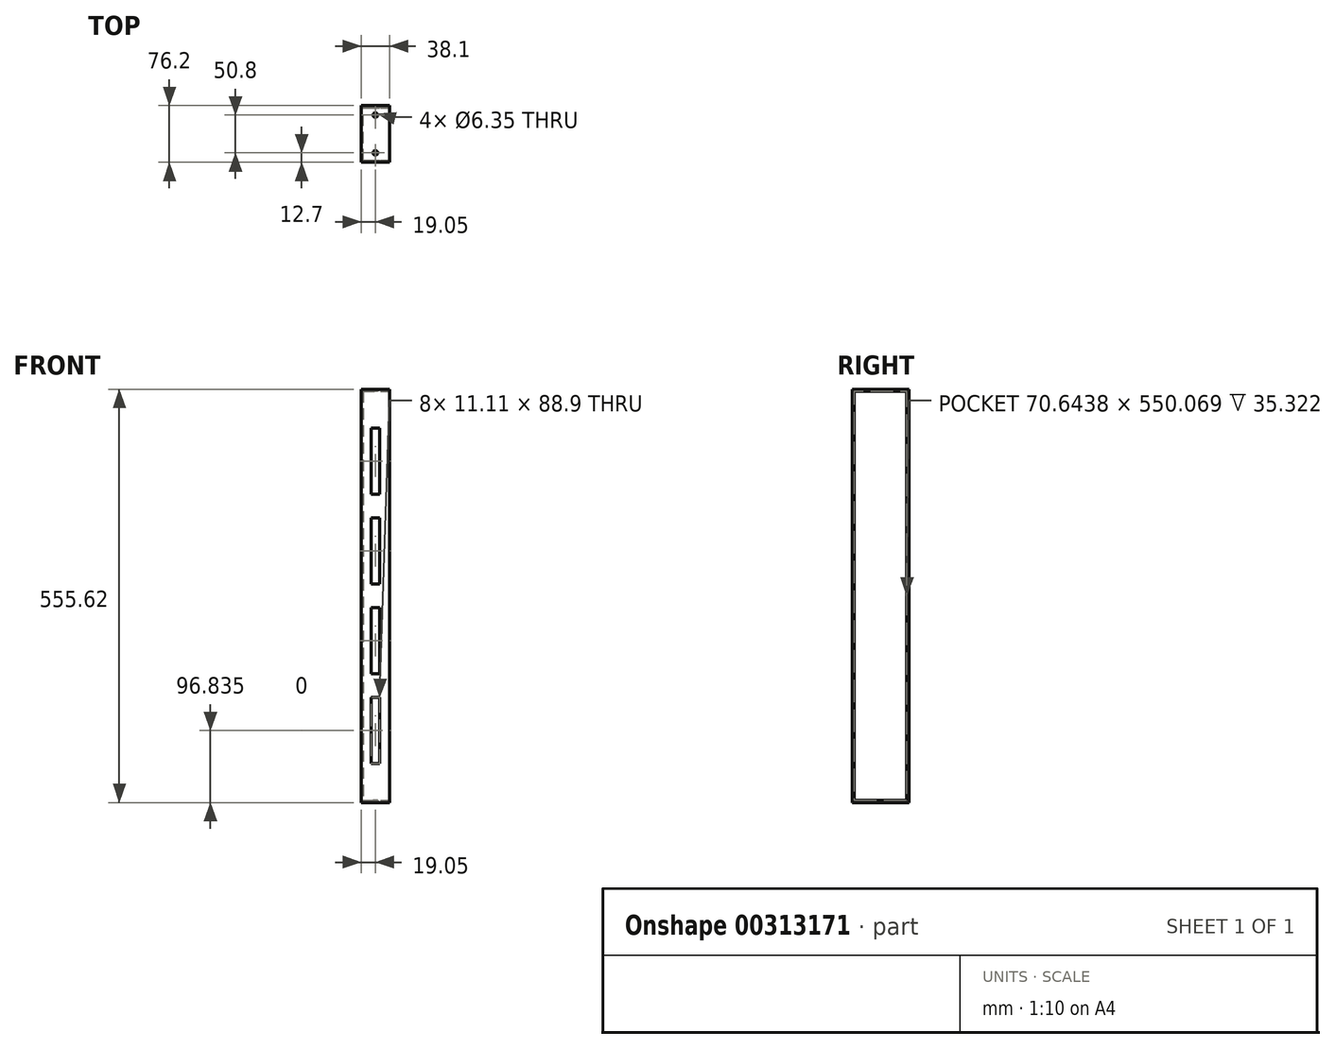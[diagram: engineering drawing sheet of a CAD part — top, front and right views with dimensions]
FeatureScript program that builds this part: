
annotation { "Feature Type Name" : "Feature", "Feature Type Description" : "" }
export const myFeature = defineFeature(function(context is Context, id is Id, definition is map)
    precondition{}
    {
        {
            var Q0;
            Q0=qCreatedBy(makeId("Top.planeOp"),FACE);
            var sketch = newSketch(context, id + "F0", { "sketchPlane" : qUnion([Q0])});
            skLineSegment(sketch, "E0.bottom", {"start": v(0, 0) * mm, "end": v(38.1, 0) * mm});
            skLineSegment(sketch, "E0.top", {"start": v(0, 76.2) * mm, "end": v(38.1, 76.2) * mm});
            skLineSegment(sketch, "E0.left", {"start": v(0, 0) * mm, "end": v(0, 76.2) * mm});
            skLineSegment(sketch, "E0.right", {"start": v(38.1, 0) * mm, "end": v(38.1, 76.2) * mm});
            skSolve(sketch);
        }
        {
            var Q0;
            Q0=qSketchRegion(id+"F0",true);
            extrude(context, id + "F1", {"entities" : qUnion([Q0]), "endBound" : BoundingType.SYMMETRIC, "depth" : 555.62 * mm});
        }
        {
            var Q0;
            Q0=makeQuery(id+"F1.opExtrude","SWEPT_FACE",FACE,{"disambiguationData":[OSD([sQuery(id+"F0.wireOp",EDGE,"E0.right")])]});
            shell(context, id + "F2", {"entities" : qUnion([Q0]), "thickness" : 2.78 * mm});
        }
        {
            var Q0;
            Q0=makeQuery(id+"F1.opExtrude","CAP_FACE",FACE,{"disambiguationData":[OSD([sQuery(id+"F0.wireOp",EDGE,"E0.bottom"),sQuery(id+"F0.wireOp",EDGE,"E0.top"),sQuery(id+"F0.wireOp",EDGE,"E0.left"),sQuery(id+"F0.wireOp",EDGE,"E0.right")])],"isStart":true});
            var sketch = newSketch(context, id + "F3", { "sketchPlane" : qUnion([Q0])});
            skCircle(sketch, "E1", {"center": v(19.05, -12.7) * mm, "radius": 3.18 * mm});
            skPoint(sketch, "E1.centerSnap0", {"position": v(19.05, 0) * mm});
            skCircle(sketch, "E2", {"center": v(19.05, -63.5) * mm, "radius": 3.18 * mm});
            skSolve(sketch);
        }
        {
            var Q0;
            Q0=qSketchRegion(id+"F3",true);
            extrude(context, id + "F4", {"entities" : qUnion([Q0]), "operationType" : NewBodyOperationType.REMOVE, "endBound" : BoundingType.THROUGH_ALL, "oppositeDirection" : true, "depth" : 25.4 * mm});
        }
        {
            var Q0;
            Q0=makeQuery(id+"F1.opExtrude","SWEPT_FACE",FACE,{"disambiguationData":[OSD([sQuery(id+"F0.wireOp",EDGE,"E0.bottom")])]});
            var sketch = newSketch(context, id + "F5", { "sketchPlane" : qUnion([Q0])});
            skLineSegment(sketch, "E3.bottom", {"start": v(24.6, -225.43) * mm, "end": v(13.5, -225.43) * mm});
            skLineSegment(sketch, "E3.top", {"start": v(24.6, -136.53) * mm, "end": v(13.5, -136.53) * mm});
            skLineSegment(sketch, "E3.left", {"start": v(24.6, -225.43) * mm, "end": v(24.6, -136.53) * mm});
            skLineSegment(sketch, "E3.right", {"start": v(13.5, -225.43) * mm, "end": v(13.5, -136.53) * mm});
            skPoint(sketch, "E3.middle", {"position": v(19.05, -180.97) * mm});
            skPoint(sketch, "E3.middle.positionSnap0", {"position": v(19.05, -277.81) * mm});
            skPoint(sketch, "E3.centerSnap0", {"position": v(19.05, -277.81) * mm});
            skLineSegment(sketch, "E4.0.1.0", {"start": v(24.6, -104.78) * mm, "end": v(13.5, -104.78) * mm});
            skPoint(sketch, "E4.0.1.1", {"position": v(19.05, -60.33) * mm});
            skLineSegment(sketch, "E4.0.1.2", {"start": v(13.5, -104.78) * mm, "end": v(13.5, -15.88) * mm});
            skLineSegment(sketch, "E4.0.1.3", {"start": v(24.6, -104.78) * mm, "end": v(24.6, -15.88) * mm});
            skLineSegment(sketch, "E4.0.1.4", {"start": v(24.6, -15.88) * mm, "end": v(13.5, -15.88) * mm});
            skLineSegment(sketch, "E4.direction1", {"start": v(13.5, -225.43) * mm, "end": v(38.1, -225.43) * mm, "construction": true});
            skLineSegment(sketch, "E4.direction2", {"start": v(13.5, -225.43) * mm, "end": v(13.5, -104.78) * mm, "construction": true});
            skPoint(sketch, "E5", {"position": v(38.1, -205.55) * mm});
            skPoint(sketch, "E6", {"position": v(38.1, 153.23) * mm});
            skLineSegment(sketch, "E7.0.0.2", {"start": v(24.6, 15.87) * mm, "end": v(13.5, 15.87) * mm});
            skPoint(sketch, "E7.3.0.2", {"position": v(19.05, 60.32) * mm});
            skLineSegment(sketch, "E7.4.0.2", {"start": v(13.5, 15.87) * mm, "end": v(13.5, 104.77) * mm});
            skLineSegment(sketch, "E7.7.0.2", {"start": v(24.6, 15.87) * mm, "end": v(24.6, 104.77) * mm});
            skLineSegment(sketch, "E7.10.0.2", {"start": v(24.6, 104.77) * mm, "end": v(13.5, 104.77) * mm});
            skLineSegment(sketch, "E7.0.0.3", {"start": v(24.6, 136.52) * mm, "end": v(13.5, 136.52) * mm});
            skPoint(sketch, "E7.3.0.3", {"position": v(19.05, 180.97) * mm});
            skLineSegment(sketch, "E7.4.0.3", {"start": v(13.5, 136.52) * mm, "end": v(13.5, 225.42) * mm});
            skLineSegment(sketch, "E7.7.0.3", {"start": v(24.6, 136.52) * mm, "end": v(24.6, 225.42) * mm});
            skLineSegment(sketch, "E7.10.0.3", {"start": v(24.6, 225.42) * mm, "end": v(13.5, 225.42) * mm});
            skSolve(sketch);
        }
        {
            var Q0;
            Q0 = qSketchRegion(id + "F5", true);
            extrude(context, id + "F6", {"entities" : qUnion([Q0]), "operationType" : NewBodyOperationType.REMOVE, "endBound" : BoundingType.THROUGH_ALL, "oppositeDirection" : true, "depth" : 25.4 * mm});
        }
    });
